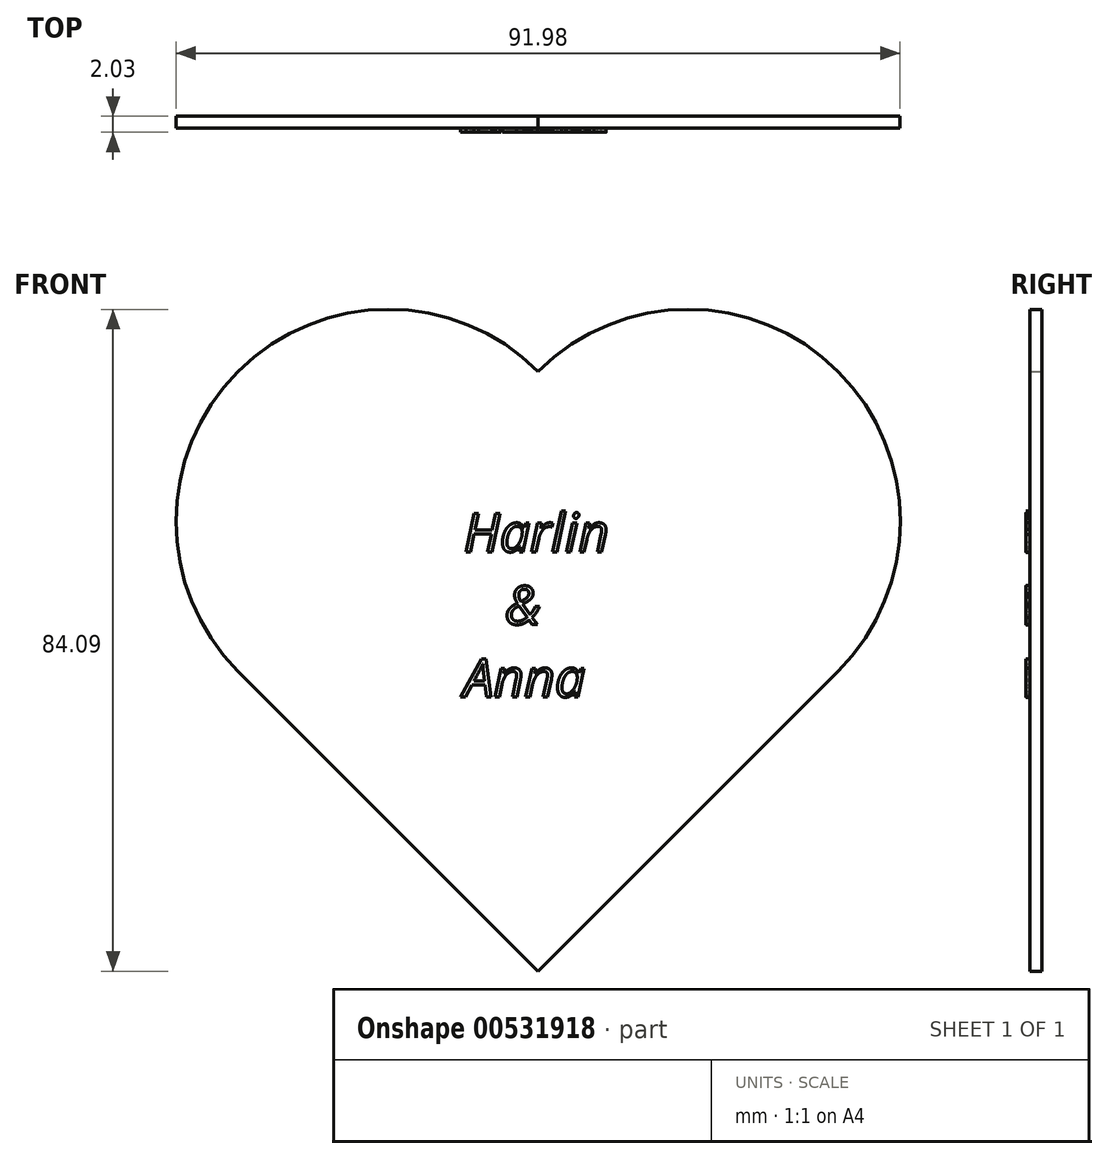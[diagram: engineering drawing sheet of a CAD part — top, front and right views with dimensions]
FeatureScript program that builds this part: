
annotation { "Feature Type Name" : "Feature", "Feature Type Description" : "" }
export const myFeature = defineFeature(function(context is Context, id is Id, definition is map)
    precondition{}
    {
        {
            var Q0;
            Q0=qCreatedBy(makeId("Front.planeOp"),FACE);
            var sketch = newSketch(context, id + "F0", { "sketchPlane" : qUnion([Q0])});
            skLineSegment(sketch, "E0", {"start": v(0, 0) * mm, "end": v(-38.1, 38.1) * mm});
            skLineSegment(sketch, "E1", {"start": v(-38.1, 38.1) * mm, "end": v(38.1, 38.1) * mm, "construction": true});
            skLineSegment(sketch, "E2", {"start": v(38.1, 38.1) * mm, "end": v(0, 0) * mm});
            skArc(sketch, "E3", {"start": v(38.1, 38.1) * mm, "mid": v(38.1, 76.2) * mm, "end": v(0, 76.2) * mm});
            skLineSegment(sketch, "E4", {"start": v(0, 0) * mm, "end": v(0, 38.1) * mm, "construction": true});
            skArc(sketch, "E5.MirrorCS", {"start": v(-38.1, 38.1) * mm, "mid": v(-38.1, 76.2) * mm, "end": v(0, 76.2) * mm});
            skPoint(sketch, "E6.orphan", {"position": v(0, 38.1) * mm});
            skSolve(sketch);
        }
        {
            var Q0;
            Q0 = qSketchRegion(id + "F0", true);
            extrude(context, id + "F1", {"entities" : qUnion([Q0]), "depth" : 1.52 * mm, "offsetDistance" : 25.4 * mm});
        }
        {
            var Q0;
            Q0=makeQuery(id+"F1.opExtrude","CAP_FACE",FACE,{"disambiguationData":[OSD([sQuery(id+"F0.wireOp",EDGE,"E0"),sQuery(id+"F0.wireOp",EDGE,"E2"),sQuery(id+"F0.wireOp",EDGE,"E5.MirrorCS"),sQuery(id+"F0.wireOp",EDGE,"E3")])],"isStart":false});
            var sketch = newSketch(context, id + "F2", { "sketchPlane" : qUnion([Q0])});
            skText(sketch, "E7", { "text": "Harlin\n   &\nAnna", "fontName": "OpenSans-Italic.ttf"});
            const initialGuessF2  = {"E7": [-0.00945, 0.05329, 1, 0, 0.00488]};
            skSetInitialGuess(sketch, initialGuessF2);
            skSolve(sketch);
        }
        {
            var Q0;
            Q0 = qSketchRegion(id + "F2", true);
            extrude(context, id + "F3", {"entities" : qUnion([Q0]), "operationType" : NewBodyOperationType.ADD, "depth" : 0.5 * mm, "offsetDistance" : 25.4 * mm});
        }
    });
